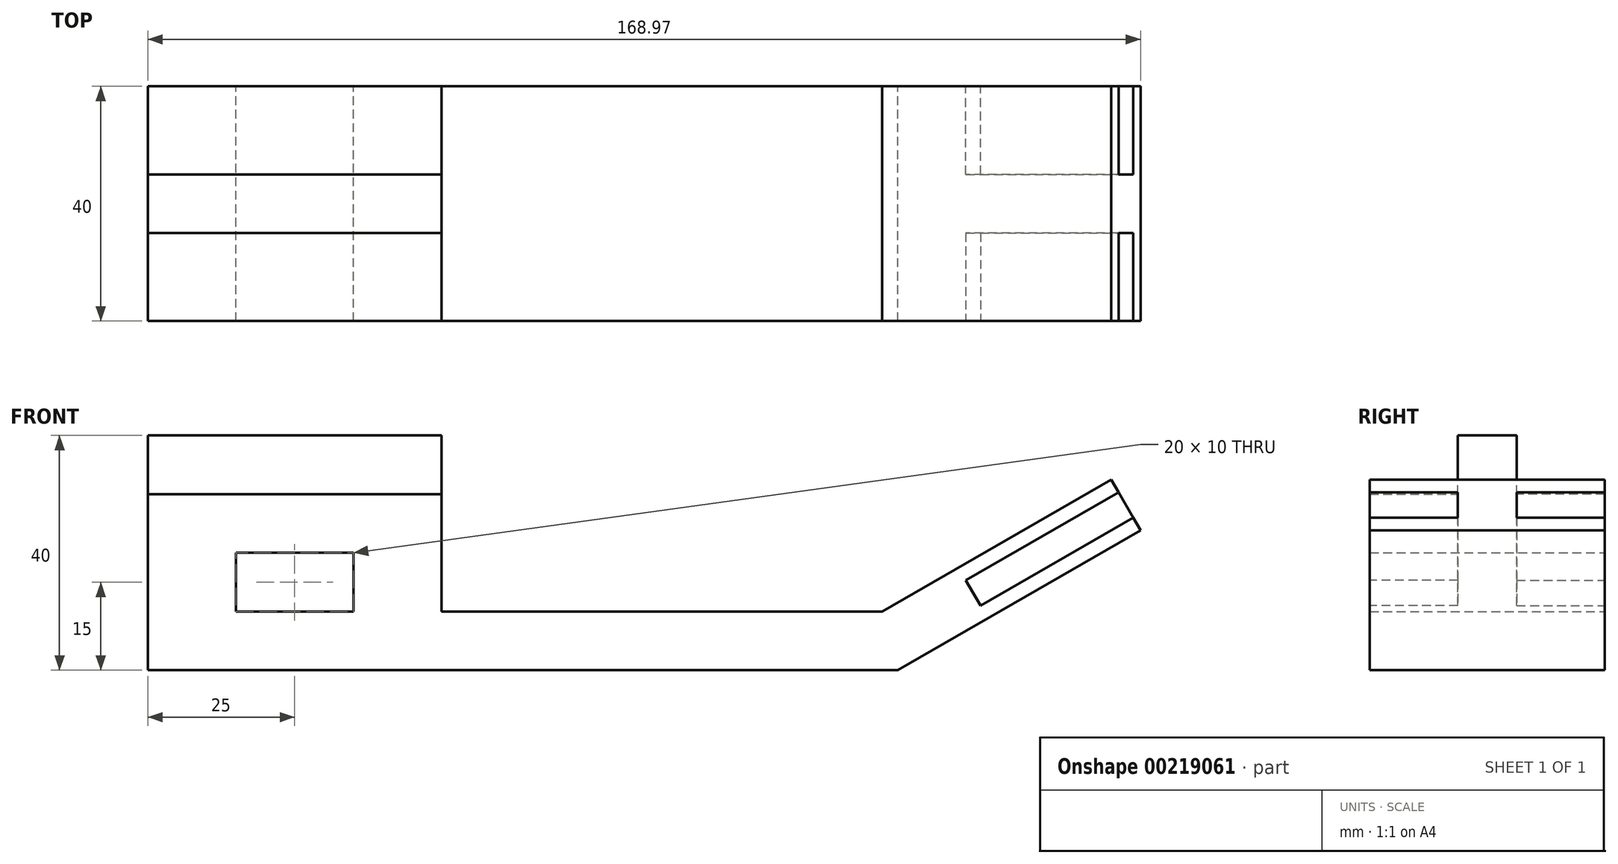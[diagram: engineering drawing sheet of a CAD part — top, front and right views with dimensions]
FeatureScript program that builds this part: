
annotation { "Feature Type Name" : "Feature", "Feature Type Description" : "" }
export const myFeature = defineFeature(function(context is Context, id is Id, definition is map)
    precondition{}
    {
        {
            var Q0;
            Q0=qCreatedBy(makeId("Front.planeOp"),FACE);
            var sketch = newSketch(context, id + "F0", { "sketchPlane" : qUnion([Q0])});
            skLineSegment(sketch, "E0", {"start": v(0, 40) * mm, "end": v(0, 0) * mm});
            skLineSegment(sketch, "E1", {"start": v(0, 0) * mm, "end": v(127.68, 0) * mm});
            skLineSegment(sketch, "E2", {"start": v(127.68, 0) * mm, "end": v(168.97, 23.84) * mm});
            skLineSegment(sketch, "E3", {"start": v(168.97, 23.84) * mm, "end": v(163.97, 32.5) * mm});
            skLineSegment(sketch, "E4", {"start": v(163.97, 32.5) * mm, "end": v(125, 10) * mm});
            skLineSegment(sketch, "E5", {"start": v(125, 10) * mm, "end": v(50, 10) * mm});
            skLineSegment(sketch, "E6", {"start": v(50, 10) * mm, "end": v(50, 40) * mm});
            skLineSegment(sketch, "E7", {"start": v(50, 40) * mm, "end": v(0, 40) * mm});
            skLineSegment(sketch, "E8", {"start": v(0, 30) * mm, "end": v(50, 30) * mm});
            skLineSegment(sketch, "E9.bottom", {"start": v(15, 20) * mm, "end": v(35, 20) * mm});
            skLineSegment(sketch, "E9.top", {"start": v(15, 10) * mm, "end": v(35, 10) * mm});
            skLineSegment(sketch, "E9.left", {"start": v(15, 20) * mm, "end": v(15, 10) * mm});
            skLineSegment(sketch, "E9.right", {"start": v(35, 20) * mm, "end": v(35, 10) * mm});
            skSolve(sketch);
        }
        {
            var Q0;
            {var subQ3=sQuery(id+"F0.wireOp",EDGE,"E1");Q0=makeQuery(id+"F0.imprint","IMPRINT",FACE,{"disambiguationData":[TD([[makeQuery(id+"F0.imprint","IMPRINT",EDGE,{"derivedFrom":subQ3}),1.0]])]});}
            extrude(context, id + "F1", {"entities" : qUnion([Q0]), "depth" : 20 * mm});
        }
        {
            var Q0;
            {var subQ0=sQuery(id+"F0.wireOp",EDGE,"E7");Q0=makeQuery(id+"F0.imprint","IMPRINT",FACE,{"disambiguationData":[TD([[makeQuery(id+"F0.imprint","IMPRINT",EDGE,{"derivedFrom":subQ0}),1.0]])]});}
            extrude(context, id + "F2", {"entities" : qUnion([Q0]), "operationType" : NewBodyOperationType.ADD, "depth" : 5 * mm});
        }
        {
            var Q0;
            Q0=makeQuery(id+"F1.opExtrude","CAP_FACE",FACE,{"disambiguationData":[OSD([sQuery(id+"F0.wireOp",EDGE,"E0"),sQuery(id+"F0.wireOp",EDGE,"E1"),sQuery(id+"F0.wireOp",EDGE,"E2"),sQuery(id+"F0.wireOp",EDGE,"E3"),sQuery(id+"F0.wireOp",EDGE,"E4"),sQuery(id+"F0.wireOp",EDGE,"E5"),sQuery(id+"F0.wireOp",EDGE,"E6"),sQuery(id+"F0.wireOp",EDGE,"E8"),sQuery(id+"F0.wireOp",EDGE,"E9.bottom"),sQuery(id+"F0.wireOp",EDGE,"E9.top"),sQuery(id+"F0.wireOp",EDGE,"E9.left"),sQuery(id+"F0.wireOp",EDGE,"E9.right")])],"isStart":false});
            var sketch = newSketch(context, id + "F3", { "sketchPlane" : qUnion([Q0])});
            skLineSegment(sketch, "E10", {"start": v(165.22, 30.33) * mm, "end": v(139.24, 15.33) * mm});
            skLineSegment(sketch, "E11", {"start": v(139.24, 15.33) * mm, "end": v(141.74, 11) * mm});
            skLineSegment(sketch, "E12", {"start": v(141.74, 11) * mm, "end": v(167.72, 26) * mm});
            skLineSegment(sketch, "E13", {"start": v(167.72, 26) * mm, "end": v(165.22, 30.33) * mm});
            skSolve(sketch);
        }
        {
            var Q0;
            Q0 = qSketchRegion(id + "F3", true);
            extrude(context, id + "F4", {"entities" : qUnion([Q0]), "operationType" : NewBodyOperationType.REMOVE, "oppositeDirection" : true, "depth" : 15 * mm});
        }
        {
            var Q0;
            Q0=makeQuery(id+"F1.opExtrude","SWEPT_BODY",BODY,{"disambiguationData":[OSD([sQuery(id+"F0.wireOp",EDGE,"E0"),sQuery(id+"F0.wireOp",EDGE,"E1"),sQuery(id+"F0.wireOp",EDGE,"E2"),sQuery(id+"F0.wireOp",EDGE,"E3"),sQuery(id+"F0.wireOp",EDGE,"E4"),sQuery(id+"F0.wireOp",EDGE,"E5"),sQuery(id+"F0.wireOp",EDGE,"E6"),sQuery(id+"F0.wireOp",EDGE,"E8"),sQuery(id+"F0.wireOp",EDGE,"E9.bottom"),sQuery(id+"F0.wireOp",EDGE,"E9.top"),sQuery(id+"F0.wireOp",EDGE,"E9.left"),sQuery(id+"F0.wireOp",EDGE,"E9.right")])]});
            var Q1;
            Q1=qCreatedBy(makeId("Front.planeOp"),FACE);
            mirror(context, id + "F5", {"operationType" : NewBodyOperationType.ADD, "entities" : qUnion([Q0]), "mirrorPlane" : qUnion([Q1])});
        }
    });
